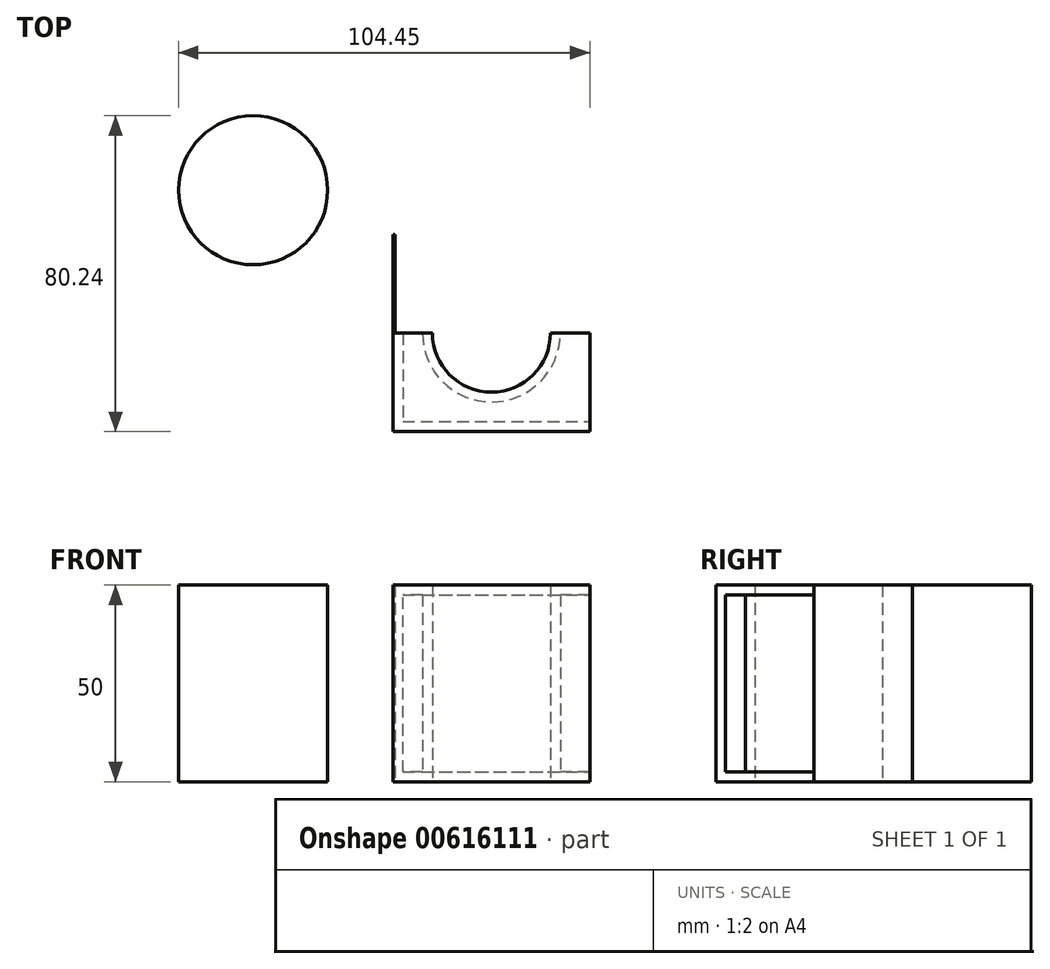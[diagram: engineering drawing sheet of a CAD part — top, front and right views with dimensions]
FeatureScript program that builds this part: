
annotation { "Feature Type Name" : "Feature", "Feature Type Description" : "" }
export const myFeature = defineFeature(function(context is Context, id is Id, definition is map)
    precondition{}
    {
        {
            var Q0;
            Q0=qCreatedBy(makeId("Top.planeOp"),FACE);
            var sketch = newSketch(context, id + "F0", { "sketchPlane" : qUnion([Q0])});
            skLineSegment(sketch, "E0.bottom", {"start": v(-25, 25) * mm, "end": v(25, 25) * mm});
            skLineSegment(sketch, "E0.top", {"start": v(-25, -25) * mm, "end": v(25, -25) * mm});
            skLineSegment(sketch, "E0.left", {"start": v(-25, 25) * mm, "end": v(-25, -25) * mm});
            skLineSegment(sketch, "E0.right", {"start": v(25, 25) * mm, "end": v(25, -25) * mm});
            skPoint(sketch, "E0.middle", {"position": v(0, 0) * mm});
            skSolve(sketch);
        }
        {
            var Q0;
            Q0 = qSketchRegion(id + "F0", true);
            extrude(context, id + "F1", {"entities" : qUnion([Q0]), "depth" : 50 * mm, "offsetDistance" : 25 * mm});
        }
        {
            var Q0;
            Q0=qCreatedBy(makeId("Top.planeOp"),FACE);
            var sketch = newSketch(context, id + "F2", { "sketchPlane" : qUnion([Q0])});
            skCircle(sketch, "E1", {"center": v(-60.52, 36.31) * mm, "radius": 18.93 * mm});
            skSolve(sketch);
        }
        {
            var Q0;
            Q0 = qSketchRegion(id + "F2", true);
            extrude(context, id + "F3", {"entities" : qUnion([Q0]), "depth" : 50 * mm, "offsetDistance" : 25 * mm});
        }
        {
            var Q0;
            Q0=qCreatedBy(makeId("Top.planeOp"),FACE);
            var sketch = newSketch(context, id + "F4", { "sketchPlane" : qUnion([Q0])});
            skCircle(sketch, "E2", {"center": v(0, 0) * mm, "radius": 15 * mm});
            skSolve(sketch);
        }
        {
            var Q0;
            Q0 = qSketchRegion(id + "F4", true);
            extrude(context, id + "F5", {"entities" : qUnion([Q0]), "operationType" : NewBodyOperationType.REMOVE, "depth" : 50 * mm, "offsetDistance" : 25 * mm});
        }
        {
            var Q0;
            Q0=makeQuery(id+"F1.opExtrude","SWEPT_FACE",FACE,{"disambiguationData":[OSD([sQuery(id+"F0.wireOp",EDGE,"E0.right")])]});
            var Q1;
            Q1=makeQuery(id+"F1.opExtrude","SWEPT_BODY",BODY,{"disambiguationData":[OSD([sQuery(id+"F0.wireOp",EDGE,"E0.bottom"),sQuery(id+"F0.wireOp",EDGE,"E0.top"),sQuery(id+"F0.wireOp",EDGE,"E0.left"),sQuery(id+"F0.wireOp",EDGE,"E0.right")])]});
            shell(context, id + "F6", {"entities" : qUnion([Q0]), "parts" : qUnion([Q1]), "thickness" : 2.5 * mm});
        }
        {
            var Q0;
            Q0=qCreatedBy(makeId("Top.planeOp"),FACE);
            var sketch = newSketch(context, id + "F7", { "sketchPlane" : qUnion([Q0])});
            skLineSegment(sketch, "E3.bottom", {"start": v(-24.54, 25) * mm, "end": v(25.46, 25) * mm});
            skLineSegment(sketch, "E3.top", {"start": v(-24.54, 0) * mm, "end": v(25.46, 0) * mm});
            skLineSegment(sketch, "E3.left", {"start": v(-24.54, 25) * mm, "end": v(-24.54, 0) * mm});
            skLineSegment(sketch, "E3.right", {"start": v(25.46, 25) * mm, "end": v(25.46, 0) * mm});
            skSolve(sketch);
        }
        {
            var Q0;
            Q0 = qSketchRegion(id + "F7", true);
            extrude(context, id + "F8", {"entities" : qUnion([Q0]), "operationType" : NewBodyOperationType.REMOVE, "depth" : 50 * mm, "offsetDistance" : 25 * mm});
        }
    });
